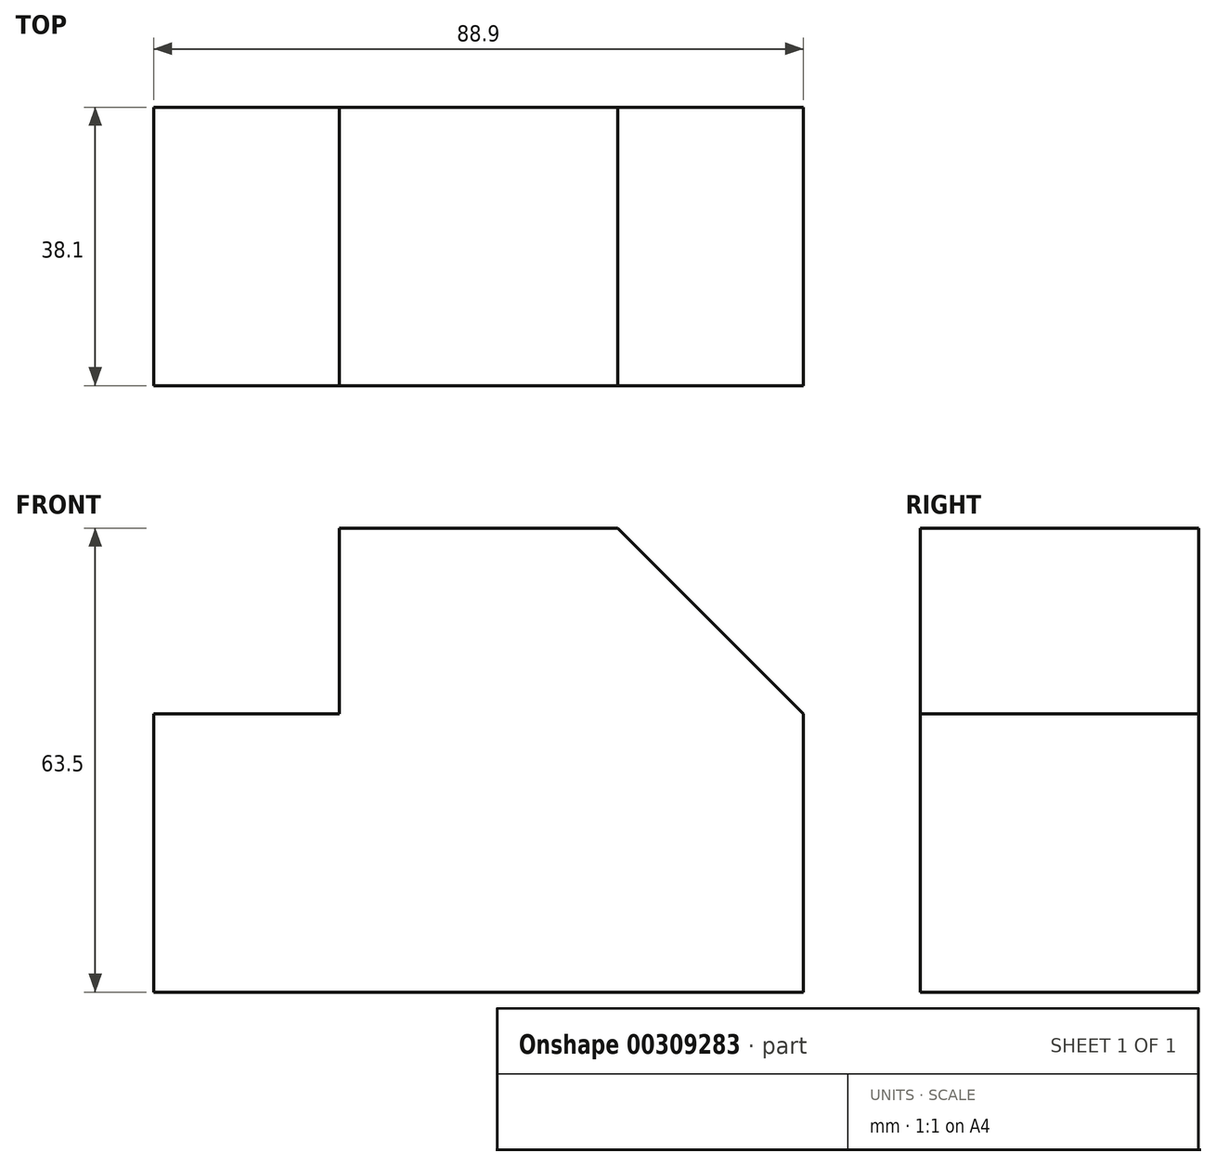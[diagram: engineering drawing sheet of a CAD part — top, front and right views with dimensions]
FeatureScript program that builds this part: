
annotation { "Feature Type Name" : "Feature", "Feature Type Description" : "" }
export const myFeature = defineFeature(function(context is Context, id is Id, definition is map)
    precondition{}
    {
        {
            var Q0;
            Q0=qCreatedBy(makeId("Front.planeOp"),FACE);
            var sketch = newSketch(context, id + "F0", { "sketchPlane" : qUnion([Q0])});
            skLineSegment(sketch, "E0", {"start": v(41.06, -52.24) * mm, "end": v(41.06, -14.14) * mm});
            skLineSegment(sketch, "E1", {"start": v(41.06, -14.14) * mm, "end": v(15.66, 11.26) * mm});
            skLineSegment(sketch, "E2", {"start": v(15.66, 11.26) * mm, "end": v(-22.44, 11.26) * mm});
            skLineSegment(sketch, "E3", {"start": v(-22.44, 11.26) * mm, "end": v(-22.44, -14.14) * mm});
            skLineSegment(sketch, "E4", {"start": v(-22.44, -14.14) * mm, "end": v(-47.84, -14.14) * mm});
            skLineSegment(sketch, "E5", {"start": v(-47.84, -14.14) * mm, "end": v(-47.84, -52.24) * mm});
            skLineSegment(sketch, "E6", {"start": v(-47.84, -52.24) * mm, "end": v(41.06, -52.24) * mm});
            skSolve(sketch);
        }
        {
            var Q0;
            Q0=makeQuery(id+"F0.imprint","IMPRINT",FACE,{"disambiguationData":[TD([[makeQuery(id+"F0.imprint","IMPRINT",EDGE,{"derivedFrom":sQuery(id+"F0.wireOp",EDGE,"E0")}),1.0]])]});
            extrude(context, id + "F1", {"entities" : qUnion([Q0]), "depth" : 38.1 * mm});
        }
    });
